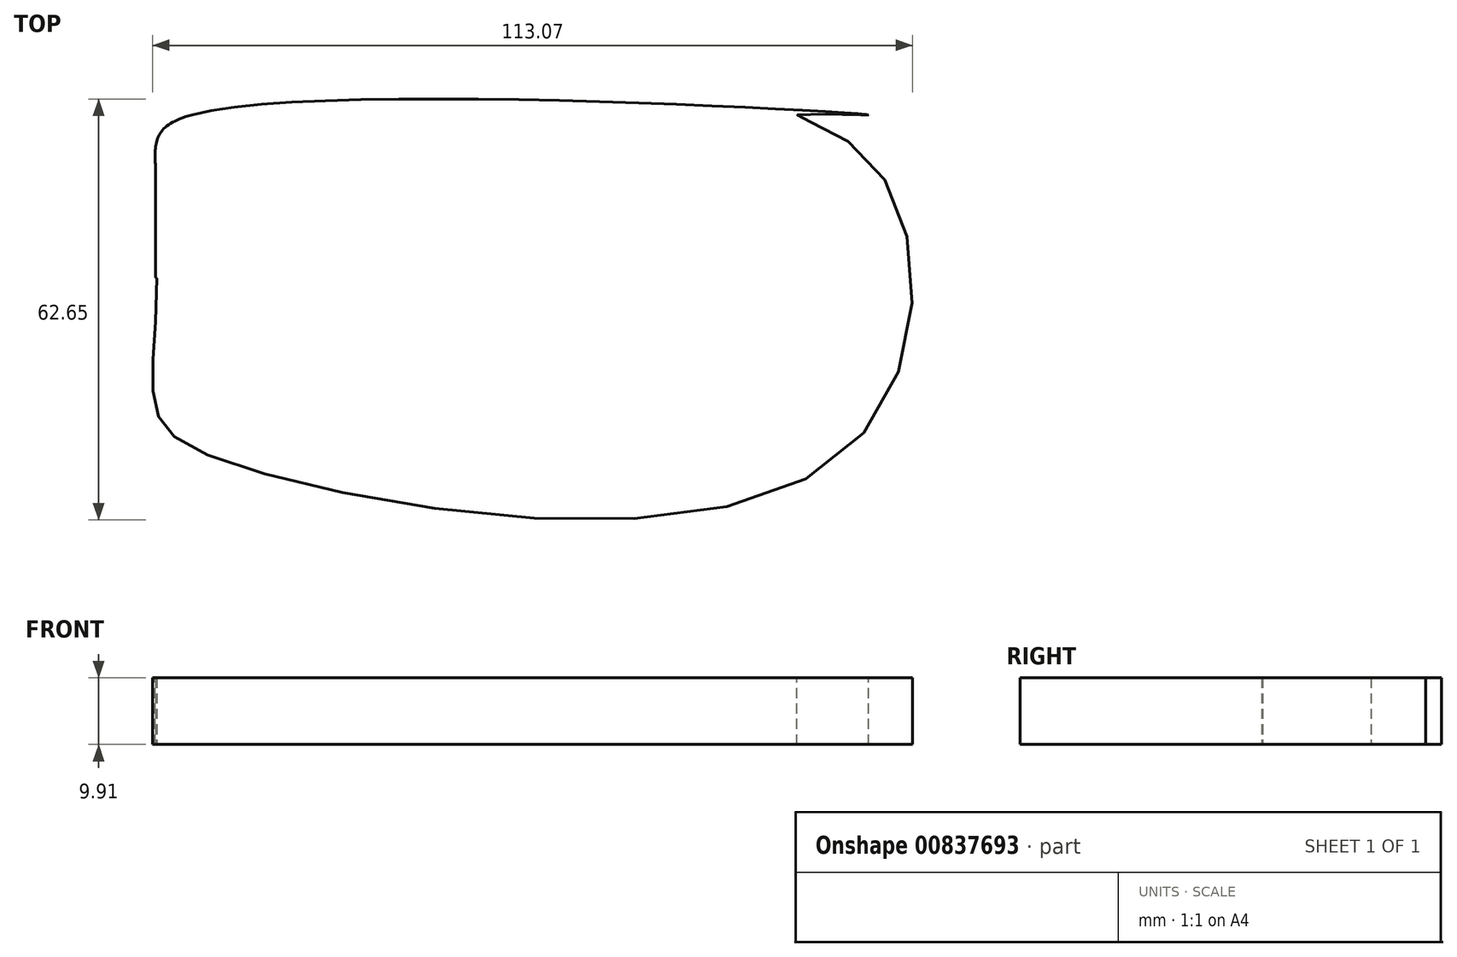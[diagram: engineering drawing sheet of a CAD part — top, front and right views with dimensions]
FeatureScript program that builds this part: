
annotation { "Feature Type Name" : "Feature", "Feature Type Description" : "" }
export const myFeature = defineFeature(function(context is Context, id is Id, definition is map)
    precondition{}
    {
        {
            var Q0;
            Q0=qCreatedBy(makeId("Top.planeOp"),FACE);
            var sketch = newSketch(context, id + "F0", { "sketchPlane" : qUnion([Q0])});
            skLineSegment(sketch, "E0.bottom", {"start": v(-54.94, 35.8) * mm, "end": v(-10.43, 35.8) * mm});
            skLineSegment(sketch, "E0.left", {"start": v(-60.36, 31.09) * mm, "end": v(-60.36, 11.58) * mm});
            skFitSpline(sketch, "E1.trimOffspring", {"points": [v(-60.36, 27.67) * mm, v(-54.94, 35.8) * mm, v(45.69, 35.8) * mm, v(35.24, 35.8) * mm, v(45.69, 29.22) * mm, v(40.66, -15.67) * mm, v(-50.3, -15.67) * mm, v(-60.36, -7.93) * mm, v(-60.36, 5.61) * mm, v(-60.36, 27.67) * mm]});
            skLineSegment(sketch, "E2", {"start": v(-10.43, 35.8) * mm, "end": v(-10.43, 11.58) * mm});
            skLineSegment(sketch, "E3", {"start": v(-60.15, 11.46) * mm, "end": v(-60.36, 11.58) * mm});
            skLineSegment(sketch, "E4", {"start": v(-60.36, 11.58) * mm, "end": v(-10.43, 11.58) * mm});
            skLineSegment(sketch, "E5.trimOffspring", {"start": v(44.53, 35.8) * mm, "end": v(45.69, 35.8) * mm});
            skSolve(sketch);
        }
        {
            var Q0;
            Q0 = qSketchRegion(id + "F0", true);
            extrude(context, id + "F1", {"entities" : qUnion([Q0]), "depth" : 9.9 * mm, "offsetDistance" : 25.4 * mm});
        }
    });
